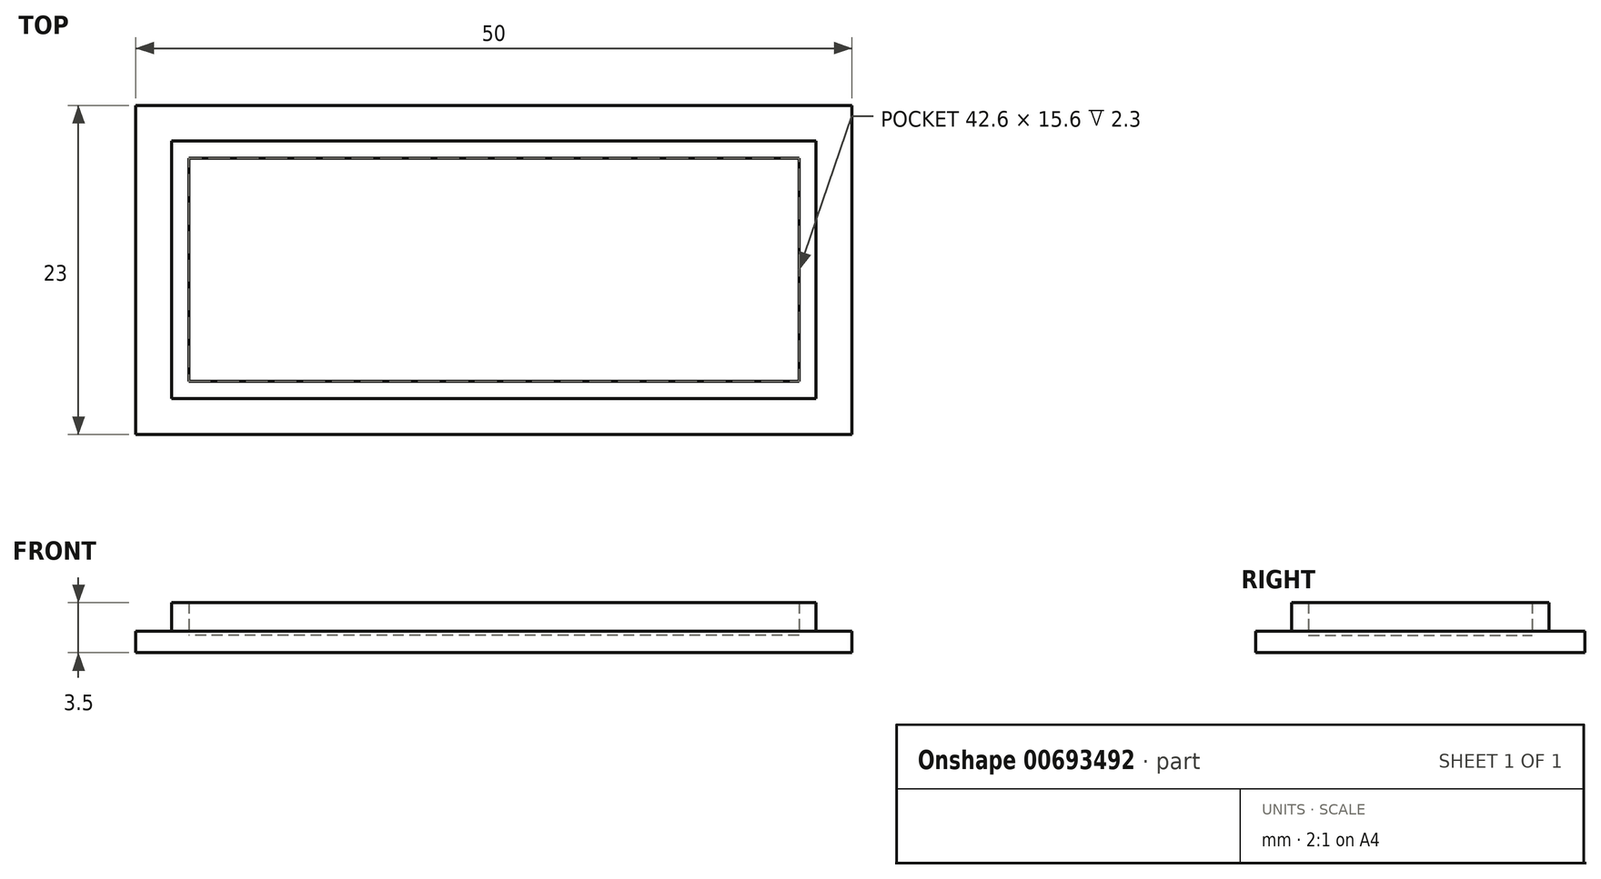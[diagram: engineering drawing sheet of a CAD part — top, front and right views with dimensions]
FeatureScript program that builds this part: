
annotation { "Feature Type Name" : "Feature", "Feature Type Description" : "" }
export const myFeature = defineFeature(function(context is Context, id is Id, definition is map)
    precondition{}
    {
        {
            var Q0;
            Q0=qCreatedBy(makeId("Top.planeOp"),FACE);
            var sketch = newSketch(context, id + "F0", { "sketchPlane" : qUnion([Q0])});
            skLineSegment(sketch, "E0.bottom", {"start": v(-25, 11.5) * mm, "end": v(25, 11.5) * mm});
            skLineSegment(sketch, "E0.top", {"start": v(-25, -11.5) * mm, "end": v(25, -11.5) * mm});
            skLineSegment(sketch, "E0.left", {"start": v(-25, 11.5) * mm, "end": v(-25, -11.5) * mm});
            skLineSegment(sketch, "E0.right", {"start": v(25, 11.5) * mm, "end": v(25, -11.5) * mm});
            skSolve(sketch);
        }
        {
            var Q0;
            Q0=makeQuery(id+"F0.imprint","IMPRINT",FACE,{"disambiguationData":[TD([[makeQuery(id+"F0.imprint","IMPRINT",EDGE,{"derivedFrom":sQuery(id+"F0.wireOp",EDGE,"E0.bottom")}),-1.0]])]});
            extrude(context, id + "F1", {"entities" : qUnion([Q0]), "depth" : 1.5 * mm, "offsetDistance" : 25 * mm});
        }
        {
            var Q0;
            Q0=makeQuery(id+"F1.opExtrude","CAP_FACE",FACE,{"disambiguationData":[OSD([sQuery(id+"F0.wireOp",EDGE,"E0.bottom"),sQuery(id+"F0.wireOp",EDGE,"E0.top"),sQuery(id+"F0.wireOp",EDGE,"E0.left"),sQuery(id+"F0.wireOp",EDGE,"E0.right")])],"isStart":false});
            var sketch = newSketch(context, id + "F2", { "sketchPlane" : qUnion([Q0])});
            skLineSegment(sketch, "E1.bottom", {"start": v(-22.5, 9) * mm, "end": v(22.5, 9) * mm});
            skLineSegment(sketch, "E1.top", {"start": v(-22.5, -9) * mm, "end": v(22.5, -9) * mm});
            skLineSegment(sketch, "E1.left", {"start": v(-22.5, 9) * mm, "end": v(-22.5, -9) * mm});
            skLineSegment(sketch, "E1.right", {"start": v(22.5, 9) * mm, "end": v(22.5, -9) * mm});
            skSolve(sketch);
        }
        {
            var Q0;
            Q0=makeQuery(id+"F2.imprint","IMPRINT",FACE,{"disambiguationData":[TD([[makeQuery(id+"F2.imprint","IMPRINT",EDGE,{"derivedFrom":sQuery(id+"F2.wireOp",EDGE,"E1.bottom")}),-1.0]])]});
            extrude(context, id + "F3", {"entities" : qUnion([Q0]), "operationType" : NewBodyOperationType.ADD, "depth" : 2 * mm, "offsetDistance" : 25 * mm});
        }
        {
            var Q0;
            Q0=makeQuery(id+"F3.opExtrude","CAP_FACE",FACE,{"disambiguationData":[OSD([sQuery(id+"F2.wireOp",EDGE,"E1.bottom"),sQuery(id+"F2.wireOp",EDGE,"E1.top"),sQuery(id+"F2.wireOp",EDGE,"E1.left"),sQuery(id+"F2.wireOp",EDGE,"E1.right")])],"isStart":false});
            shell(context, id + "F4", {"entities" : qUnion([Q0]), "thickness" : 1.2 * mm});
        }
    });
